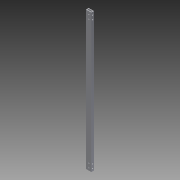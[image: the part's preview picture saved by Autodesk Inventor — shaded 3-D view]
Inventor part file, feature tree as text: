
AUTODESK INVENTOR PART (.ipt)
format: ipt  version: 2013 (Build 170138000, 138)  size: 329,216 bytes
history: native  units: in
note: dims shown in document units (in); Inventor stores cm internally (conversion verified against a paired STEP export)
features: extrude x3, sketch x3, plane x1, reference x1
ambient origin geometry x8: Origin, YZ Plane, XZ Plane, XY Plane, X Axis, Y Axis, Z Axis, Center Point
bodies: Solid1 (feature_tree)
feature tree (8):
  extrude  "Extrusion1"  Depth=0.125in
  extrude  "Extrusion2"  Depth=0.5in
  plane  "Work Plane1"
  extrude  "Extrusion3"  Depth=0.25in
  sketch  "Sketch1"  dims[d0=1.0in d2=0.125in]
  sketch  "Sketch2"  dims[d3=26.0in d4=0.0in d5=0.5in]
  reference  "Reference1"
  sketch  "Sketch3"  dims[d6=1.0in d7=0.0in d8=0.25in d10=0.5in d11=0.75in d12=0.5in d13=0.75in d14=1.0in d15=0.0in]
